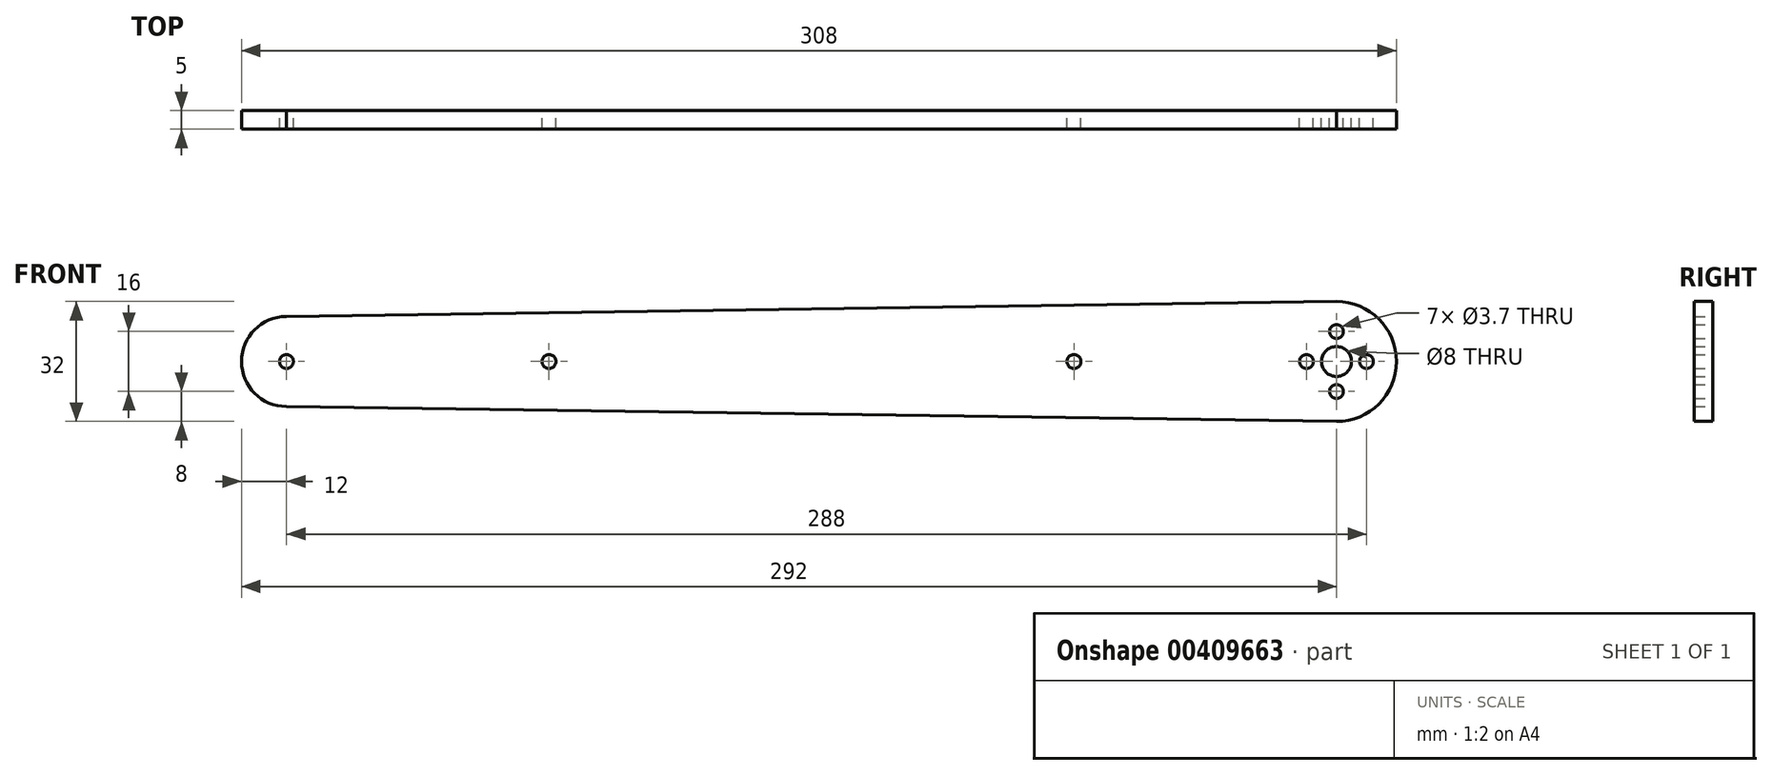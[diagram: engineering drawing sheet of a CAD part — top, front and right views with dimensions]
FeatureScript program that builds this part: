
annotation { "Feature Type Name" : "Feature", "Feature Type Description" : "" }
export const myFeature = defineFeature(function(context is Context, id is Id, definition is map)
    precondition{}
    {
        {
            var Q0;
            Q0=qCreatedBy(makeId("Front.planeOp"),FACE);
            var sketch = newSketch(context, id + "F0", { "sketchPlane" : qUnion([Q0])});
            skPoint(sketch, "E0.middle", {"position": v(0, 0) * mm});
            skCircle(sketch, "E1", {"center": v(-140, 0) * mm, "radius": 1.85 * mm});
            skCircle(sketch, "E2", {"center": v(140, 0) * mm, "radius": 4 * mm});
            skCircle(sketch, "E3", {"center": v(140, 8) * mm, "radius": 1.85 * mm});
            skCircle(sketch, "E4.1.0", {"center": v(132, 0) * mm, "radius": 1.85 * mm});
            skCircle(sketch, "E4.2.0", {"center": v(140, -8) * mm, "radius": 1.85 * mm});
            skCircle(sketch, "E4.3.0", {"center": v(148, 0) * mm, "radius": 1.85 * mm});
            skCircle(sketch, "E5", {"center": v(-70, 0) * mm, "radius": 1.85 * mm});
            skCircle(sketch, "E6", {"center": v(70, 0) * mm, "radius": 1.85 * mm});
            skArc(sketch, "E7", {"start": v(-140, -12) * mm, "mid": v(-152, 0) * mm, "end": v(-140, 12) * mm});
            skArc(sketch, "E8", {"start": v(140, -16) * mm, "mid": v(156, 0) * mm, "end": v(140, 16) * mm});
            skLineSegment(sketch, "E9", {"start": v(-140, 12) * mm, "end": v(140, 16) * mm});
            skLineSegment(sketch, "E10", {"start": v(140, -16) * mm, "end": v(-140, -12) * mm});
            skSolve(sketch);
        }
        {
            var Q0;
            Q0=makeQuery(id+"F0.imprint","IMPRINT",FACE,{"disambiguationData":[TD([[makeQuery(id+"F0.imprint","IMPRINT",EDGE,{"derivedFrom":sQuery(id+"F0.wireOp",EDGE,"E1")}),-1.0]])]});
            extrude(context, id + "F1", {"entities" : qUnion([Q0]), "endBound" : BoundingType.SYMMETRIC, "depth" : 5 * mm});
        }
    });
